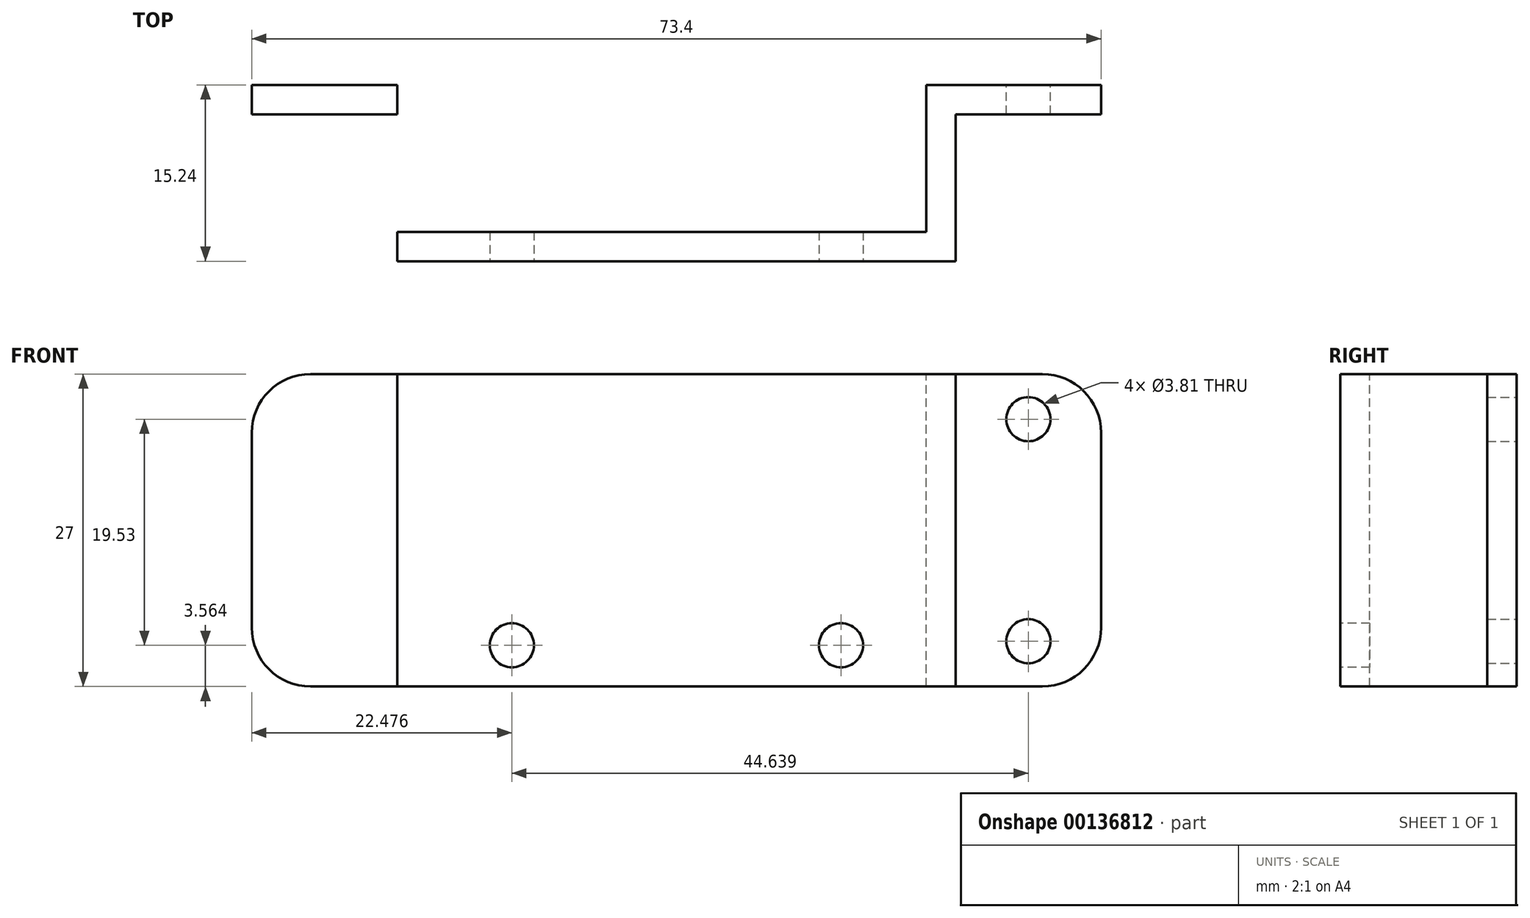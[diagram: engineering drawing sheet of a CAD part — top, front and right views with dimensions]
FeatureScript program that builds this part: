
annotation { "Feature Type Name" : "Feature", "Feature Type Description" : "" }
export const myFeature = defineFeature(function(context is Context, id is Id, definition is map)
    precondition{}
    {
        {
            var Q0;
            Q0=qCreatedBy(makeId("Top.planeOp"),FACE);
            var sketch = newSketch(context, id + "F0", { "sketchPlane" : qUnion([Q0])});
            skLineSegment(sketch, "E0.bottom", {"start": v(24.13, 1.27) * mm, "end": v(-24.13, 1.27) * mm});
            skLineSegment(sketch, "E0.top", {"start": v(24.13, -1.27) * mm, "end": v(-24.13, -1.27) * mm});
            skLineSegment(sketch, "E0.left", {"start": v(24.13, 1.27) * mm, "end": v(24.13, -1.27) * mm});
            skLineSegment(sketch, "E0.right", {"start": v(-24.13, 1.27) * mm, "end": v(-24.13, -1.27) * mm});
            skPoint(sketch, "E0.middle", {"position": v(0, 0) * mm});
            skLineSegment(sketch, "E1.bottom", {"start": v(-24.13, 1.27) * mm, "end": v(-21.59, 1.27) * mm});
            skLineSegment(sketch, "E1.top", {"start": v(-24.13, 13.97) * mm, "end": v(-21.59, 13.97) * mm});
            skLineSegment(sketch, "E1.left", {"start": v(-24.13, 1.27) * mm, "end": v(-24.13, 13.97) * mm});
            skLineSegment(sketch, "E1.right", {"start": v(-21.59, 1.27) * mm, "end": v(-21.59, 13.97) * mm});
            skLineSegment(sketch, "E2.bottom", {"start": v(-24.13, 13.97) * mm, "end": v(-36.7, 13.97) * mm});
            skLineSegment(sketch, "E2.top", {"start": v(-24.13, 11.43) * mm, "end": v(-36.7, 11.43) * mm});
            skLineSegment(sketch, "E2.left", {"start": v(-24.13, 13.97) * mm, "end": v(-24.13, 11.43) * mm});
            skLineSegment(sketch, "E2.right", {"start": v(-36.7, 13.97) * mm, "end": v(-36.7, 11.43) * mm});
            skLineSegment(sketch, "E3.MirrorCS", {"start": v(21.59, 1.27) * mm, "end": v(21.59, 13.97) * mm});
            skLineSegment(sketch, "E4.MirrorCS", {"start": v(24.13, 1.27) * mm, "end": v(24.13, 13.97) * mm});
            skLineSegment(sketch, "E5.MirrorCS", {"start": v(24.13, 13.97) * mm, "end": v(21.59, 13.97) * mm});
            skLineSegment(sketch, "E6.MirrorCS", {"start": v(24.13, 13.97) * mm, "end": v(36.7, 13.97) * mm});
            skLineSegment(sketch, "E7.MirrorCS", {"start": v(24.13, 11.43) * mm, "end": v(36.7, 11.43) * mm});
            skLineSegment(sketch, "E8.MirrorCS", {"start": v(36.7, 13.97) * mm, "end": v(36.7, 11.43) * mm});
            skSolve(sketch);
        }
        {
            var Q0;
            Q0=makeQuery(id+"F0.imprint","IMPRINT",FACE,{"disambiguationData":[TD([[makeQuery(id+"F0.imprint","IMPRINT",EDGE,{"derivedFrom":sQuery(id+"F0.wireOp",EDGE,"E2.bottom")}),1.0]])]});
            var Q1;
            Q1=makeQuery(id+"F0.imprint","IMPRINT",FACE,{"disambiguationData":[TD([[makeQuery(id+"F0.imprint","IMPRINT",EDGE,{"derivedFrom":sQuery(id+"F0.wireOp",EDGE,"E1.bottom")}),1.0]])]});
            var Q2;
            Q2=makeQuery(id+"F0.imprint","IMPRINT",FACE,{"disambiguationData":[TD([[makeQuery(id+"F0.imprint","IMPRINT",EDGE,{"derivedFrom":sQuery(id+"F0.wireOp",EDGE,"E0.top")}),-1.0]])]});
            var Q3;
            {var subQ5=sQuery(id+"F0.wireOp",EDGE,"E3.MirrorCS");Q3=makeQuery(id+"F0.imprint","IMPRINT",FACE,{"disambiguationData":[TD([[makeQuery(id+"F0.imprint","IMPRINT",EDGE,{"derivedFrom":subQ5}),-1.0]])]});}
            var Q4;
            {var subQ0=sQuery(id+"F0.wireOp",EDGE,"E6.MirrorCS");Q4=makeQuery(id+"F0.imprint","IMPRINT",FACE,{"disambiguationData":[TD([[makeQuery(id+"F0.imprint","IMPRINT",EDGE,{"derivedFrom":subQ0}),-1.0]])]});}
            extrude(context, id + "F1", {"entities" : qUnion([Q0, Q1, Q2, Q3, Q4]), "endBound" : BoundingType.SYMMETRIC, "oppositeDirection" : true, "depth" : 27 * mm});
        }
        {
            var Q0;
            Q0=makeQuery(id+"F1.opExtrude","SWEPT_FACE",FACE,{"disambiguationData":[OSD([sQuery(id+"F0.wireOp",EDGE,"E2.top")])]});
            var sketch = newSketch(context, id + "F2", { "sketchPlane" : qUnion([Q0])});
            skLineSegment(sketch, "E9", {"start": v(-30.42, 11.5) * mm, "end": v(-30.42, -13.5) * mm});
            skLineSegment(sketch, "E10.MirrorCS", {"start": v(-30.42, -11.5) * mm, "end": v(-30.42, 13.5) * mm});
            skLineSegment(sketch, "E11.MirrorCS", {"start": v(30.42, 11.5) * mm, "end": v(30.42, -13.5) * mm});
            skLineSegment(sketch, "E12.MirrorCS", {"start": v(30.42, -11.5) * mm, "end": v(30.42, 13.5) * mm});
            skSolve(sketch);
        }
        {
            var Q0;
            Q0=makeQuery(id+"F1.opExtrude","SWEPT_FACE",FACE,{"disambiguationData":[OSD([sQuery(id+"F0.wireOp",EDGE,"E0.top")])]});
            var sketch = newSketch(context, id + "F3", { "sketchPlane" : qUnion([Q0])});
            skLineSegment(sketch, "E13.bottom", {"start": v(14.22, 13.72) * mm, "end": v(-14.22, 13.72) * mm});
            skLineSegment(sketch, "E13.top", {"start": v(14.22, -13.72) * mm, "end": v(-14.22, -13.72) * mm});
            skLineSegment(sketch, "E13.left", {"start": v(14.22, 13.72) * mm, "end": v(14.22, -13.72) * mm});
            skLineSegment(sketch, "E13.right", {"start": v(-14.22, 13.72) * mm, "end": v(-14.22, -13.72) * mm});
            skPoint(sketch, "E13.middle", {"position": v(0, 0) * mm});
            skSolve(sketch);
        }
        {
            var Q0;
            Q0=makeQuery(id+"F0.imprint","IMPRINT",FACE,{"disambiguationData":[TD([[makeQuery(id+"F0.imprint","IMPRINT",EDGE,{"derivedFrom":sQuery(id+"F0.wireOp",EDGE,"E0.top")}),-1.0]])]});
            extrude(context, id + "F4", {"entities" : qUnion([Q0]), "operationType" : NewBodyOperationType.ADD, "depth" : (1.4 - (1.14 / 2)) * mm});
        }
        {
            var Q0;
            Q0=makeQuery(id+"F1.opExtrude","SWEPT_FACE",FACE,{"disambiguationData":[OSD([sQuery(id+"F0.wireOp",EDGE,"E5.MirrorCS"),sQuery(id+"F0.wireOp",EDGE,"E6.MirrorCS")])]});
            var sketch = newSketch(context, id + "F5", { "sketchPlane" : qUnion([Q0])});
            skLineSegment(sketch, "E14.bottom", {"start": v(30.42, 9.6) * mm, "end": v(-30.42, 9.6) * mm});
            skLineSegment(sketch, "E14.top", {"start": v(30.42, -9.6) * mm, "end": v(-30.42, -9.6) * mm});
            skLineSegment(sketch, "E14.left", {"start": v(30.42, 9.6) * mm, "end": v(30.42, -9.6) * mm});
            skLineSegment(sketch, "E14.right", {"start": v(-30.42, 9.6) * mm, "end": v(-30.42, -9.6) * mm});
            skPoint(sketch, "E14.middle", {"position": v(0, 0) * mm});
            skSolve(sketch);
        }
        {
            var Q0;
            {var subQ0=sQuery(id+"F0.wireOp",EDGE,"E0.top");Q0=makeQuery(id+"F4.boolean.opBoolean","MERGE",FACE,{"derivedFrom":[makeQuery(id+"F1.opExtrude","SWEPT_FACE",FACE,{"disambiguationData":[OSD([subQ0])]}),makeQuery(id+"F4.opExtrude","SWEPT_FACE",FACE,{"disambiguationData":[OSD([subQ0])]})]});}
            var sketch = newSketch(context, id + "F6", { "sketchPlane" : qUnion([Q0])});
            skLineSegment(sketch, "E15", {"start": v(-24.13, 3.78) * mm, "end": v(24.13, 3.78) * mm});
            skLineSegment(sketch, "E16", {"start": v(0, 21.06) * mm, "end": v(0, 3.78) * mm});
            skLineSegment(sketch, "E17.bottom", {"start": v(14.22, 17.5) * mm, "end": v(-14.22, 17.5) * mm});
            skLineSegment(sketch, "E17.top", {"start": v(14.22, -9.94) * mm, "end": v(-14.22, -9.94) * mm});
            skLineSegment(sketch, "E17.left", {"start": v(14.22, 17.5) * mm, "end": v(14.22, -9.94) * mm});
            skLineSegment(sketch, "E17.right", {"start": v(-14.22, 17.5) * mm, "end": v(-14.22, -9.94) * mm});
            skPoint(sketch, "E17.middle", {"position": v(0, 3.78) * mm});
            skSolve(sketch);
        }
        {
            var Q0;
            Q0=sQuery(id+"F5.wireOp",VERTEX,"E14.right.start");
            var Q1;
            Q1=sQuery(id+"F5.wireOp",VERTEX,"E14.right.end");
            var Q2;
            Q2=sQuery(id+"F5.wireOp",VERTEX,"E14.left.end");
            var Q3;
            Q3=sQuery(id+"F5.wireOp",VERTEX,"E14.left.start");
            var Q4;
            Q4=sQuery(id+"F6.wireOp",VERTEX,"E17.bottom.end");
            var Q5;
            Q5=sQuery(id+"F6.wireOp",VERTEX,"E17.bottom.start");
            var Q6;
            Q6=sQuery(id+"F6.wireOp",VERTEX,"E17.top.start");
            var Q7;
            Q7=sQuery(id+"F6.wireOp",VERTEX,"E17.top.end");
            var Q8;
            Q8=makeQuery(id+"F1.opExtrude","SWEPT_BODY",BODY,{"disambiguationData":[OSD([sQuery(id+"F0.wireOp",EDGE,"E0.bottom"),sQuery(id+"F0.wireOp",EDGE,"E0.top"),sQuery(id+"F0.wireOp",EDGE,"E0.left"),sQuery(id+"F0.wireOp",EDGE,"E0.right"),sQuery(id+"F0.wireOp",EDGE,"E1.top"),sQuery(id+"F0.wireOp",EDGE,"E1.left"),sQuery(id+"F0.wireOp",EDGE,"E1.right"),sQuery(id+"F0.wireOp",EDGE,"E2.bottom"),sQuery(id+"F0.wireOp",EDGE,"E2.top"),sQuery(id+"F0.wireOp",EDGE,"E2.right"),sQuery(id+"F0.wireOp",EDGE,"E3.MirrorCS"),sQuery(id+"F0.wireOp",EDGE,"E4.MirrorCS"),sQuery(id+"F0.wireOp",EDGE,"E5.MirrorCS"),sQuery(id+"F0.wireOp",EDGE,"E6.MirrorCS"),sQuery(id+"F0.wireOp",EDGE,"E7.MirrorCS"),sQuery(id+"F0.wireOp",EDGE,"E8.MirrorCS")])]});
            hole(context, id + "F7", {"style" : HoleStyle.SIMPLE, "endStyle" : HoleEndStyle.THROUGH, "holeDiameter" : 3.8 * mm, "locations" : qUnion([Q0, Q1, Q2, Q3, Q4, Q5, Q6, Q7]), "scope" : qUnion([Q8]), "isTappedThrough" : true});
        }
        {
            var Q0;
            Q0=makeQuery(id+"F1.opExtrude","CAP_EDGE",EDGE,{"disambiguationData":[OSD([sQuery(id+"F0.wireOp",EDGE,"E8.MirrorCS")])],"isStart":true});
            var Q1;
            Q1=makeQuery(id+"F1.opExtrude","CAP_EDGE",EDGE,{"disambiguationData":[OSD([sQuery(id+"F0.wireOp",EDGE,"E8.MirrorCS")])],"isStart":false});
            var Q2;
            Q2=makeQuery(id+"F1.opExtrude","CAP_EDGE",EDGE,{"disambiguationData":[OSD([sQuery(id+"F0.wireOp",EDGE,"E2.right")])],"isStart":true});
            var Q3;
            Q3=makeQuery(id+"F4.opExtrude","CAP_EDGE",EDGE,{"disambiguationData":[OSD([sQuery(id+"F0.wireOp",EDGE,"E0.right")])],"isStart":false});
            var Q4;
            Q4=makeQuery(id+"F1.opExtrude","CAP_EDGE",EDGE,{"disambiguationData":[OSD([sQuery(id+"F0.wireOp",EDGE,"E2.right")])],"isStart":false});
            var Q5;
            Q5=makeQuery(id+"F4.opExtrude","CAP_EDGE",EDGE,{"disambiguationData":[OSD([sQuery(id+"F0.wireOp",EDGE,"E0.left")])],"isStart":false});
            fillet(context, id + "F8", {"entities" : qUnion([Q0, Q1, Q2, Q3, Q4, Q5]), "radius" : 5.08 * mm, "tangentPropagation" : true, "allowEdgeOverflow" : false});
        }
    });
